# Revit family: 94811-005
name_source: partatom
category: Modelos genéricos
revit_build: Autodesk Revit 2016 (Build: 20150220_1215(x64)
units: mm (PartAtom-declared; Revit-internal decimal feet)

## family parameters
Com base no plano de trabalho = Não
Compartilhado = Não
Corte com vazios quando carregados = Não
Cota do conector redondo = Utilizar diâmetro
Pode hospedar o vergalhão = Não
Ponto de cálculo do ambiente = Não
Sempre na vertical = Sim
Tipo de parte = Normal

## types (2) — shared parameters
Comentários de tipos = Ler Manual de Instalação
Código de montagem = 94811/005
Descrição = Basic 90 - 94811/005
Desenvolvedor = Factory Cursos & Desenvolvimento
Fabricante = Tramontina
Nivel de Ruido = 55 db
Numero de Velocidades = 3
Referencia = 94811-005
Site do desenvolvedor = www.factorycursos.com.br
Tipo de imagem = <Nenhum>
URL = www.tramontina.com.br
Vazão Maxima = 380 m3/h

## per-type parameters (varying)
| type | Tensão |
| BASIC 90 - 94811-005 | 127 |
| Basic 90 - 94811-006 | 220  [stored 0.721785 ft] |

note: [stored X ft] marks values corroborated as IEEE doubles in the binary element streams (Revit-internal decimal feet)
